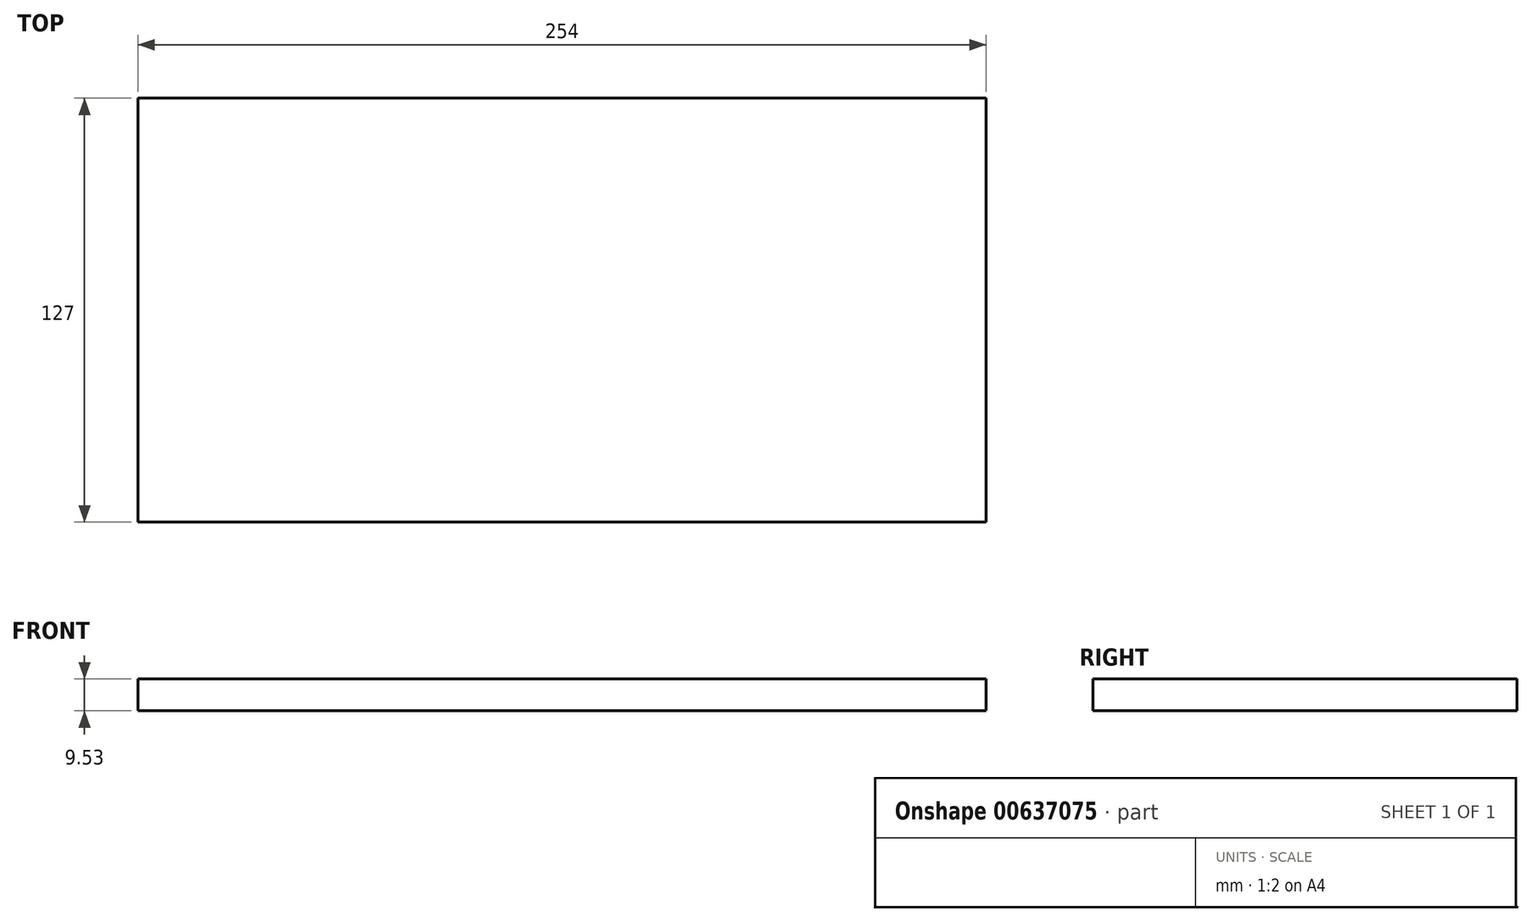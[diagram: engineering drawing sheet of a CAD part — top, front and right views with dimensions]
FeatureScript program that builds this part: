
annotation { "Feature Type Name" : "Feature", "Feature Type Description" : "" }
export const myFeature = defineFeature(function(context is Context, id is Id, definition is map)
    precondition{}
    {
        {
            var Q0;
            Q0=qCreatedBy(makeId("Top.planeOp"),FACE);
            var sketch = newSketch(context, id + "F0", { "sketchPlane" : qUnion([Q0])});
            skLineSegment(sketch, "E0.bottom", {"start": v(-41.18, 4.37) * mm, "end": v(212.82, 4.37) * mm});
            skLineSegment(sketch, "E0.top", {"start": v(-41.18, 131.37) * mm, "end": v(212.82, 131.37) * mm});
            skLineSegment(sketch, "E0.left", {"start": v(-41.18, 4.37) * mm, "end": v(-41.18, 131.37) * mm});
            skLineSegment(sketch, "E0.right", {"start": v(212.82, 4.37) * mm, "end": v(212.82, 131.37) * mm});
            skSolve(sketch);
        }
        {
            var Q0;
            Q0=makeQuery(id+"F0.imprint","IMPRINT",FACE,{"disambiguationData":[TD([[makeQuery(id+"F0.imprint","IMPRINT",EDGE,{"derivedFrom":sQuery(id+"F0.wireOp",EDGE,"E0.bottom")}),1.0]])]});
            extrude(context, id + "F1", {"entities" : qUnion([Q0]), "depth" : 9.52 * mm, "offsetDistance" : 25.4 * mm});
        }
    });
